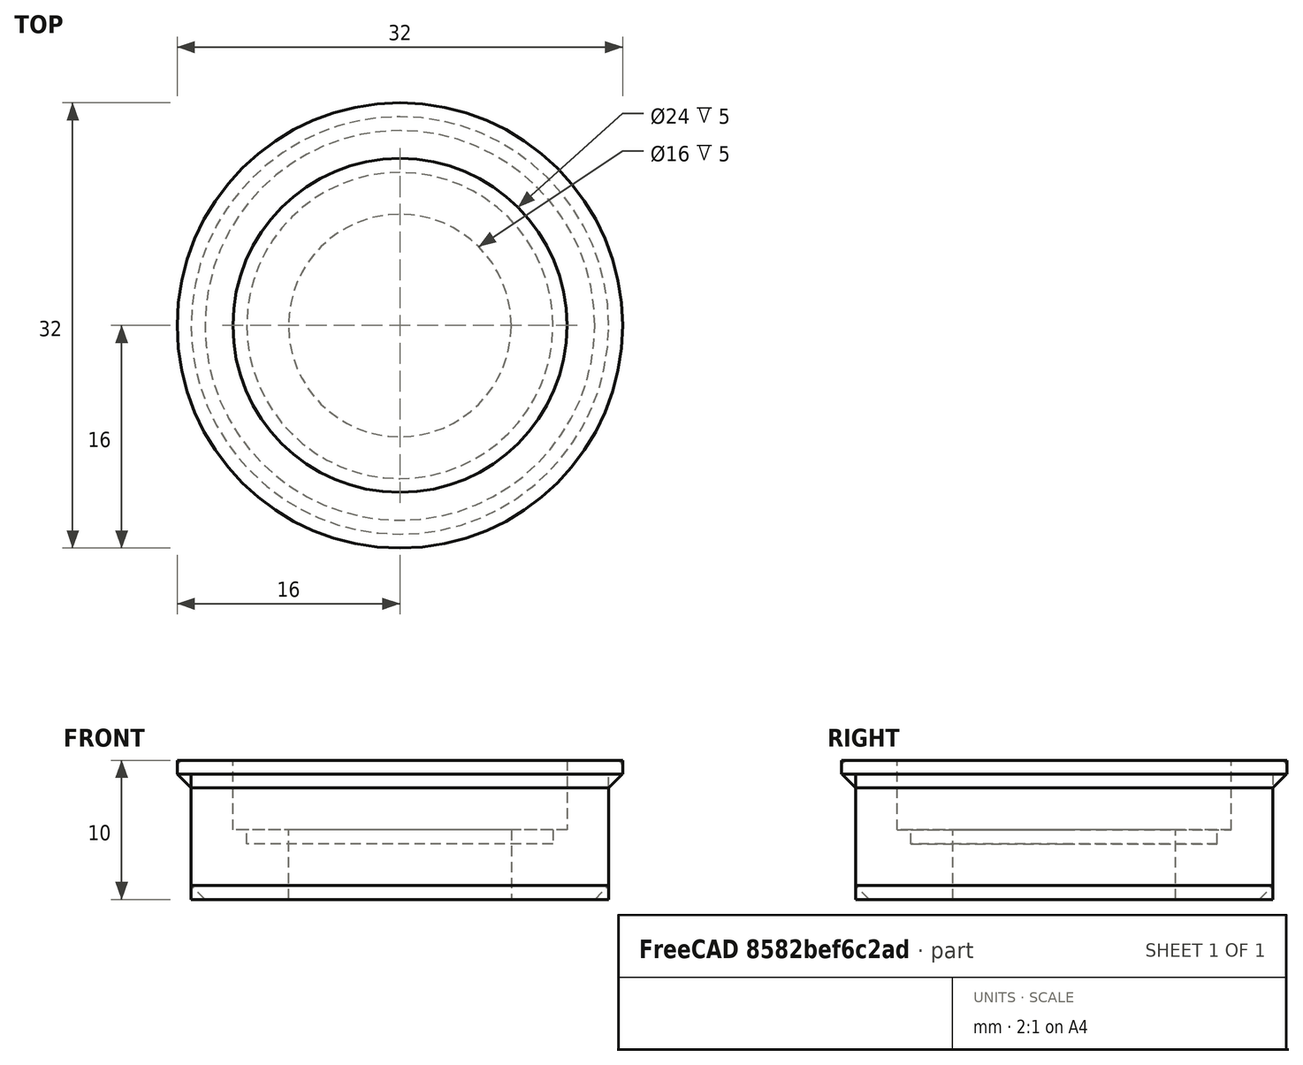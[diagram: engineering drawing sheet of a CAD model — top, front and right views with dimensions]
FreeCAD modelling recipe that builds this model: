
FCSTD DOCUMENT  (FreeCAD 0.16R)
Label: Spacer24mmto30mm
License: All rights reserved
LicenseURL: http://en.wikipedia.org/wiki/All_rights_reserved
objects: Sketcher::SketchObject×5, PartDesign::Pocket×3, PartDesign::Pad×2, PartDesign::Chamfer×2, PartDesign::Fillet×1, Mesh::Feature×1
note: 18 computed .brp shape members not serialized (recipe doc carries the construction recipe); baked Part::Feature solids carry a one-line shape summary decoded from their .brp

FEATURE [Sketcher::SketchObject] Sketch
  sketch-geometry (1):
    g0: Circle CenterX=0 CenterY=0 CenterZ=0 NormalX=0 NormalY=0 NormalZ=1 Radius=15
  constraints (2):
    c: Coincident(g0,g-1)
    c: Radius(g0) = 15
FEATURE [PartDesign::Pad] Pad
  Length = 9
  Length2 = 100
  Sketch = -> Sketch
  Type = 0
FEATURE [Sketcher::SketchObject] Sketch001
  Placement = pos=(0,0,9) rot=(0,0,1;0rad)
  Support = -> Pad [Face3]
  sketch-geometry (1):
    g0: Circle CenterX=0 CenterY=0 CenterZ=0 NormalX=0 NormalY=0 NormalZ=1 Radius=16
  constraints (2):
    c: Coincident(g-1,g0)
    c: Radius(g0) = 16
FEATURE [PartDesign::Pad] Pad001
  Length = 1
  Length2 = 100
  Sketch = -> Sketch001
  Type = 0
FEATURE [Sketcher::SketchObject] Sketch002
  Placement = pos=(0,0,10) rot=(0,0,1;0rad)
  Support = -> Pad001 [Face5]
  sketch-geometry (1):
    g0: Circle CenterX=0 CenterY=0 CenterZ=0 NormalX=0 NormalY=0 NormalZ=1 Radius=12
  constraints (2):
    c: Coincident(g0,g-1)
    c: Radius(g0) = 12
FEATURE [PartDesign::Pocket] Pocket
  Length = 5
  Sketch = -> Sketch002
  Type = 0
FEATURE [Sketcher::SketchObject] Sketch003
  Placement = pos=(0,0,5) rot=(0,0,1;0rad)
  Support = -> Pocket [Face7]
  sketch-geometry (1):
    g0: Circle CenterX=0 CenterY=0 CenterZ=0 NormalX=0 NormalY=0 NormalZ=1 Radius=8
  constraints (2):
    c: Coincident(g0,g-1)
    c: Radius(g0) = 8
FEATURE [PartDesign::Pocket] Pocket001
  Length = 5
  Sketch = -> Sketch003
  Type = 1
FEATURE [PartDesign::Chamfer] Chamfer
  Base = -> Pocket001 [Edge1]
  Size = 1
FEATURE [PartDesign::Chamfer] Chamfer001
  Base = -> Chamfer [Edge8]
  Size = 0.98
FEATURE [PartDesign::Fillet] Fillet
  Base = -> Chamfer001 [Edge11]
  Radius = 0.5
FEATURE [Sketcher::SketchObject] Sketch004
  Placement = pos=(0,0,5) rot=(0,0,1;0rad)
  Support = -> Fillet [Face8]
  sketch-geometry (1):
    g0: Circle CenterX=0 CenterY=0 CenterZ=0 NormalX=0 NormalY=0 NormalZ=1 Radius=11
  constraints (2):
    c: Coincident(g0,g-1)
    c: Radius(g0) = 11
FEATURE [PartDesign::Pocket] Pocket002
  Length = 1
  Sketch = -> Sketch004
  Type = 0
FEATURE [Mesh::Feature] Mesh  label="Pocket002 (Meshed)"
